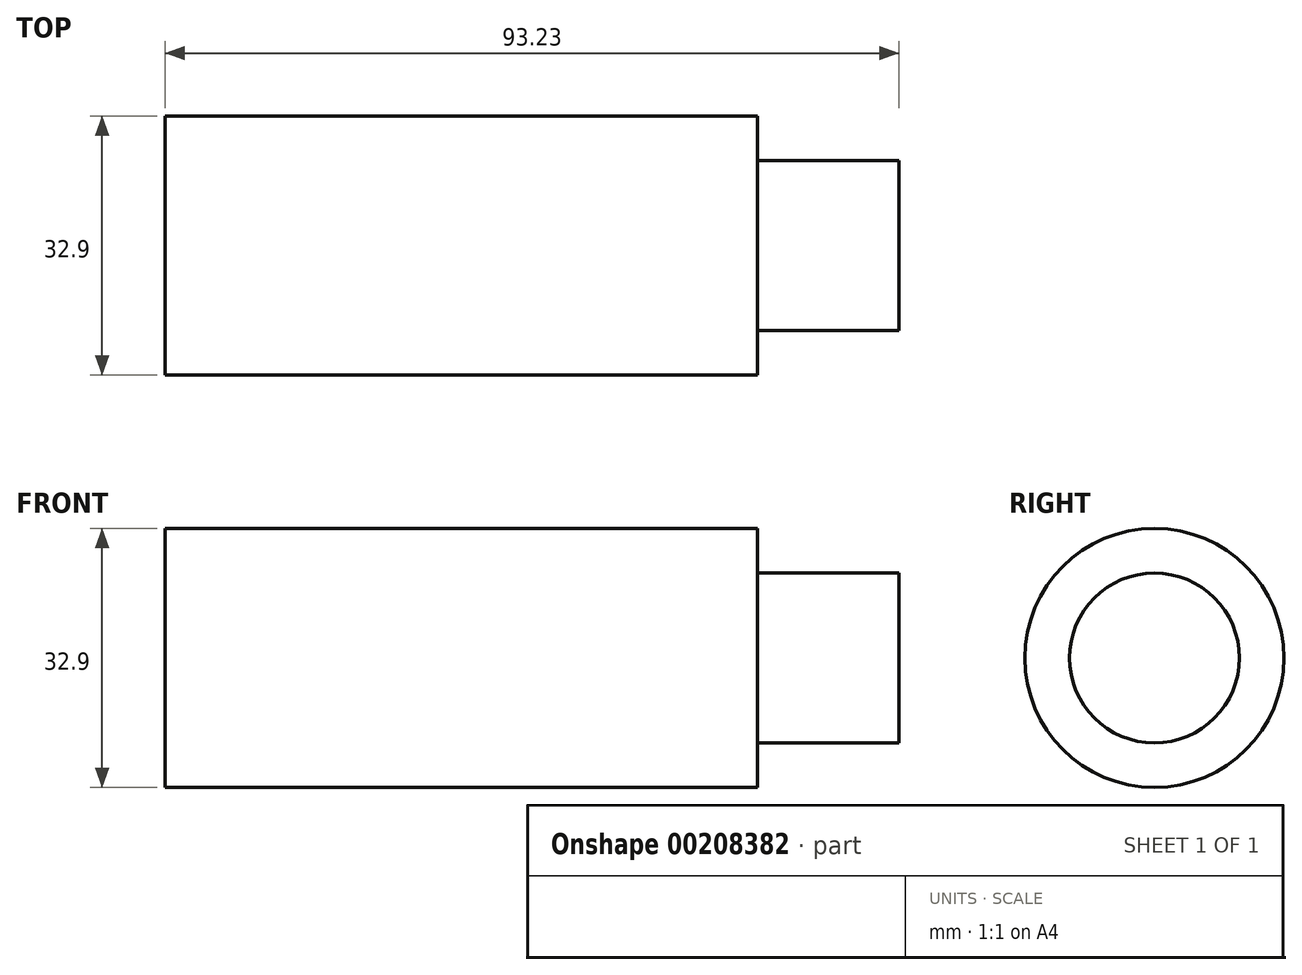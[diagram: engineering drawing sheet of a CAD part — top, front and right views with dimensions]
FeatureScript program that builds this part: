
annotation { "Feature Type Name" : "Feature", "Feature Type Description" : "" }
export const myFeature = defineFeature(function(context is Context, id is Id, definition is map)
    precondition{}
    {
        {
            var Q0;
            Q0=qCreatedBy(makeId("Front.planeOp"),FACE);
            var sketch = newSketch(context, id + "F0", { "sketchPlane" : qUnion([Q0])});
            skLineSegment(sketch, "E0", {"start": v(0, 0) * mm, "end": v(93.23, 0) * mm});
            skLineSegment(sketch, "E1", {"start": v(75.27, 16.45) * mm, "end": v(0, 16.45) * mm});
            skLineSegment(sketch, "E2", {"start": v(0, 16.45) * mm, "end": v(0, 0) * mm});
            skLineSegment(sketch, "E3", {"start": v(75.27, 16.45) * mm, "end": v(75.27, 10.8) * mm});
            skLineSegment(sketch, "E4", {"start": v(93.23, 0) * mm, "end": v(93.23, 10.8) * mm});
            skLineSegment(sketch, "E5", {"start": v(93.23, 10.8) * mm, "end": v(75.27, 10.8) * mm});
            skSolve(sketch);
        }
        {
            var Q0;
            Q0=makeQuery(id+"F0.imprint","IMPRINT",FACE,{"disambiguationData":[TD([[makeQuery(id+"F0.imprint","IMPRINT",EDGE,{"derivedFrom":sQuery(id+"F0.wireOp",EDGE,"E0")}),1.0]])]});
            var Q1;
            Q1=sQuery(id+"F0.wireOp",EDGE,"E0");
            revolve(context, id + "F1", {"entities" : qUnion([Q0]), "axis" : qUnion([Q1]), "revolveType" : RevolveType.FULL});
        }
    });
